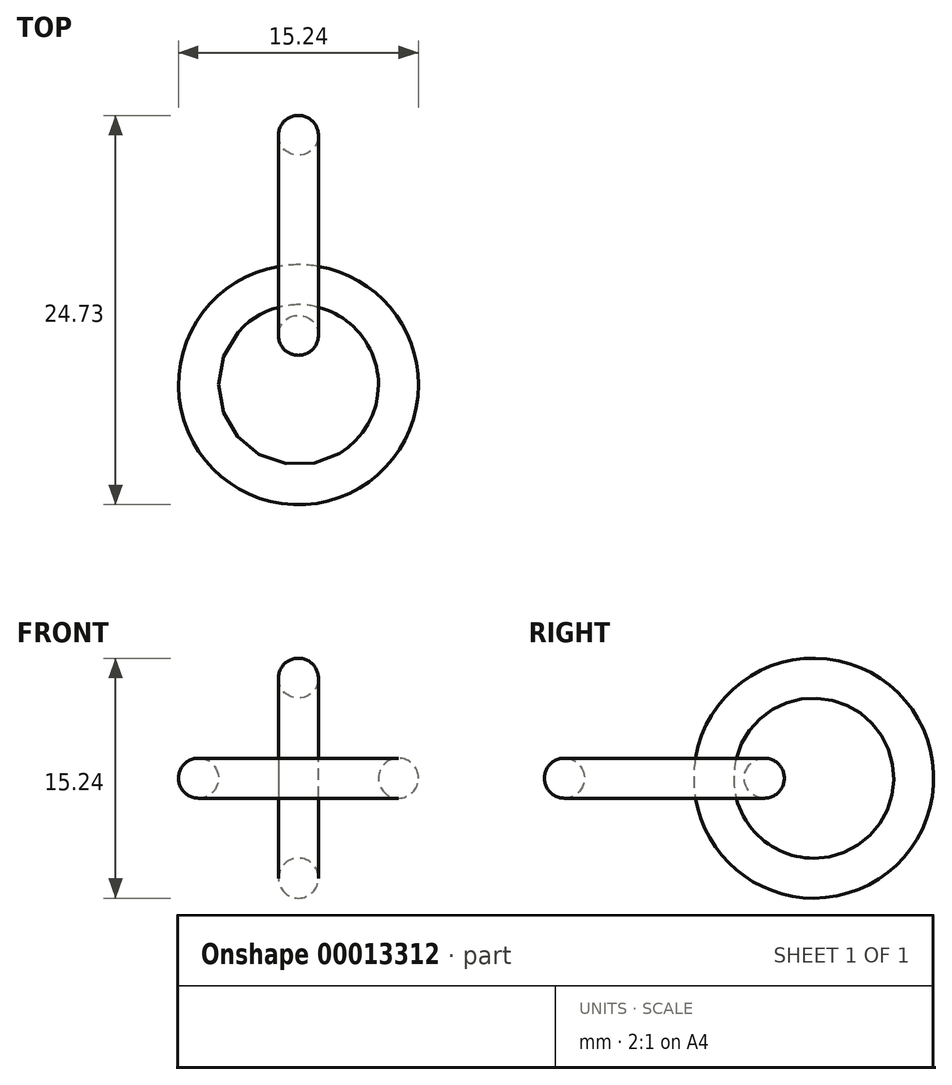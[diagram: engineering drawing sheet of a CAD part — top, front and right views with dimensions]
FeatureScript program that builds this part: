
annotation { "Feature Type Name" : "Feature", "Feature Type Description" : "" }
export const myFeature = defineFeature(function(context is Context, id is Id, definition is map)
    precondition{}
    {
        {
            var Q0;
            Q0=qCreatedBy(makeId("Top.planeOp"),FACE);
            var sketch = newSketch(context, id + "F0", { "sketchPlane" : qUnion([Q0])});
            skCircle(sketch, "E0", {"center": v(0, 0) * mm, "radius": 6.35 * mm});
            skSolve(sketch);
        }
        {
            var Q0;
            Q0=qCreatedBy(makeId("Front.planeOp"),FACE);
            var sketch = newSketch(context, id + "F1", { "sketchPlane" : qUnion([Q0])});
            skLineSegment(sketch, "E1.0", {"start": v(-6.35, 0) * mm, "end": v(6.35, 0) * mm});
            skCircle(sketch, "E2", {"center": v(6.35, 0) * mm, "radius": 1.27 * mm});
            skSolve(sketch);
        }
        {
            var Q0;
            Q0=makeQuery(id+"F1.imprint","IMPRINT",FACE,{"disambiguationData":[TD([[makeQuery(id+"F1.imprint","IMPRINT",EDGE,{"derivedFrom":sQuery(id+"F1.wireOp",EDGE,"E2")}),1.0]])]});
            var Q1;
            Q1=sQuery(id+"F0.wireOp",EDGE,"E0");
            sweep(context, id + "F2", {"profiles" : qUnion([Q0]), "path" : qUnion([Q1])});
        }
        {
            var Q0;
            Q0=qCreatedBy(makeId("Top.planeOp"),FACE);
            var sketch = newSketch(context, id + "F3", { "sketchPlane" : qUnion([Q0])});
            skCircle(sketch, "E3.cCircle", {"center": v(0, 0) * mm, "radius": 2.54 * mm, "construction": true});
            skLineSegment(sketch, "E3.0", {"start": v(-2.99, 0.97) * mm, "end": v(0, 3.14) * mm, "construction": true});
            skLineSegment(sketch, "E3.1", {"start": v(0, 3.14) * mm, "end": v(2.99, 0.97) * mm, "construction": true});
            skLineSegment(sketch, "E3.2", {"start": v(2.99, 0.97) * mm, "end": v(1.85, -2.54) * mm, "construction": true});
            skLineSegment(sketch, "E3.3", {"start": v(1.85, -2.54) * mm, "end": v(-1.85, -2.54) * mm, "construction": true});
            skLineSegment(sketch, "E3.4", {"start": v(-1.85, -2.54) * mm, "end": v(-2.99, 0.97) * mm, "construction": true});
            skPoint(sketch, "E3.0.midPoint", {"position": v(-1.5, 2.05) * mm});
            skLineSegment(sketch, "E4", {"start": v(0, 0) * mm, "end": v(0, 12.27) * mm, "construction": true});
            skCircle(sketch, "E5", {"center": v(2.99, 0.97) * mm, "radius": 1.27 * mm});
            skCircle(sketch, "E6", {"center": v(0, 3.14) * mm, "radius": 1.27 * mm});
            skCircle(sketch, "E7", {"center": v(-2.99, 0.97) * mm, "radius": 1.27 * mm});
            skCircle(sketch, "E8", {"center": v(-1.85, -2.54) * mm, "radius": 1.27 * mm});
            skCircle(sketch, "E9", {"center": v(1.85, -2.54) * mm, "radius": 1.27 * mm});
            skSolve(sketch);
        }
        {
            var Q0;
            Q0=qCreatedBy(makeId("Right.planeOp"),FACE);
            var sketch = newSketch(context, id + "F4", { "sketchPlane" : qUnion([Q0])});
            skLineSegment(sketch, "E10", {"start": v(0, 0) * mm, "end": v(17.15, 0) * mm, "construction": true});
            skLineSegment(sketch, "E11", {"start": v(9.49, -3.36) * mm, "end": v(9.49, 4.52) * mm, "construction": true});
            skCircle(sketch, "E12", {"center": v(9.49, 0) * mm, "radius": 6.35 * mm});
            skSolve(sketch);
        }
        {
            var Q0;
            Q0=makeQuery(id+"F3.imprint","IMPRINT",FACE,{"disambiguationData":[TD([[makeQuery(id+"F3.imprint","IMPRINT",EDGE,{"derivedFrom":sQuery(id+"F3.wireOp",EDGE,"E6")}),1.0]])]});
            var Q1;
            Q1=sQuery(id+"F4.wireOp",EDGE,"E12");
            sweep(context, id + "F5", {"operationType" : NewBodyOperationType.ADD, "profiles" : qUnion([Q0]), "path" : qUnion([Q1])});
        }
    });
